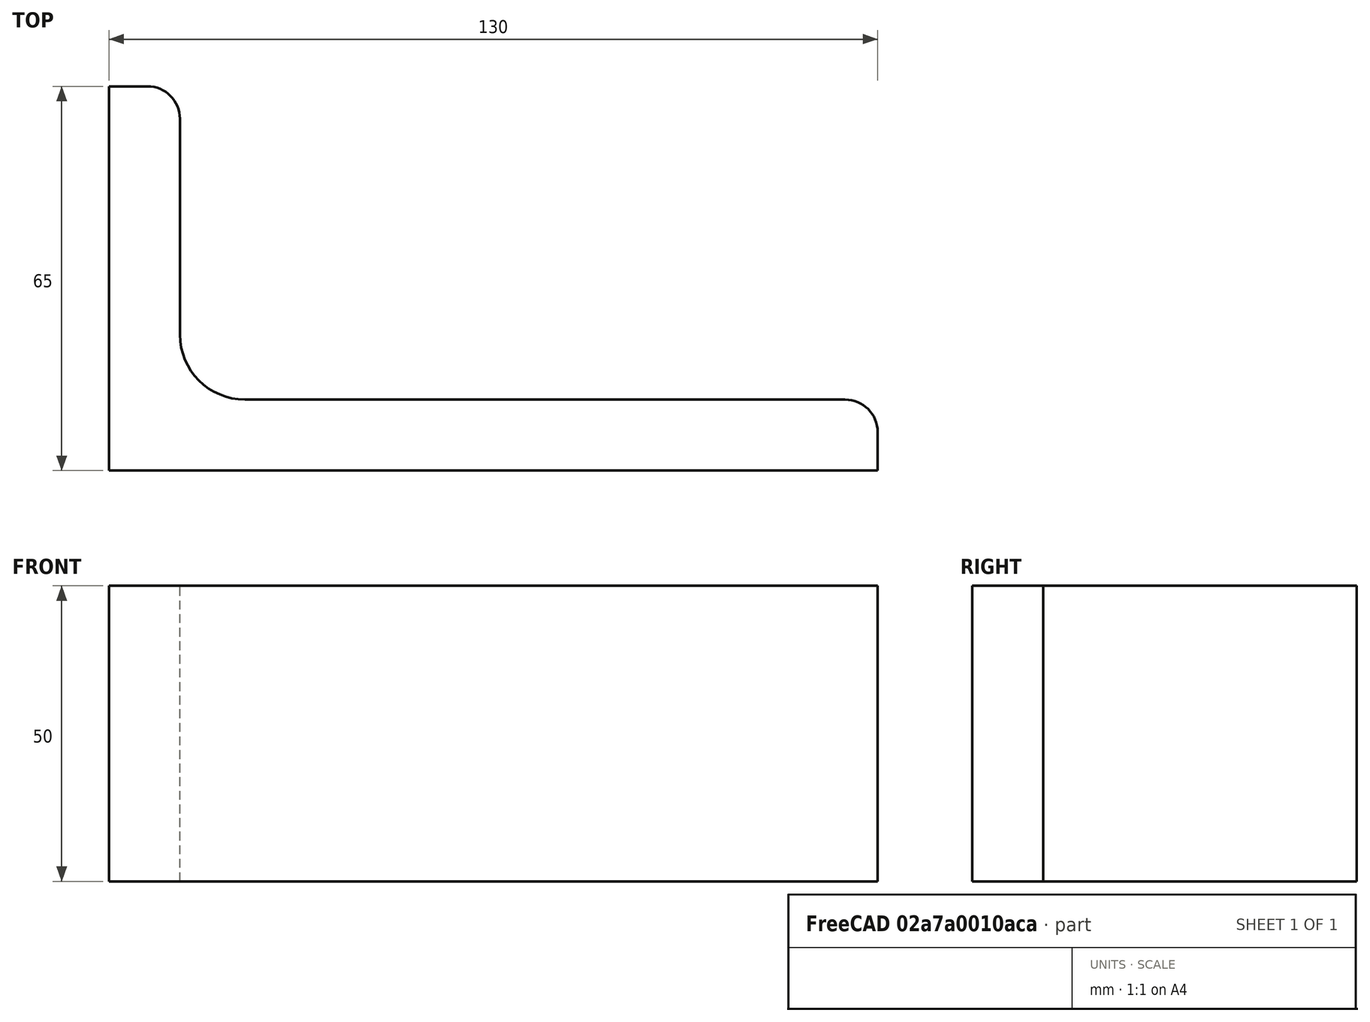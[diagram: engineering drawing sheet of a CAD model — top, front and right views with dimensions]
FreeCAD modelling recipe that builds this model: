
FCSTD DOCUMENT  (FreeCAD 0.15R4671 (Git))
Label: Angle Bar 130x65x12 EN10056 S235JR
License: All rights reserved
LicenseURL: http://en.wikipedia.org/wiki/All_rights_reserved
objects: Sketcher::SketchObject×1, Part::Extrusion×1
note: 2 computed .brp shape members not serialized (recipe doc carries the construction recipe); baked Part::Feature solids carry a one-line shape summary decoded from their .brp

FEATURE [Sketcher::SketchObject] Sketch
  sketch-geometry (9):
    g0: LineSegment StartX=0 StartY=0 StartZ=0 EndX=130 EndY=0 EndZ=0
    g1: LineSegment StartX=130 StartY=0 StartZ=0 EndX=130 EndY=6.5 EndZ=0
    g2: LineSegment StartX=124.5 StartY=12 StartZ=0 EndX=23 EndY=12 EndZ=0
    g3: LineSegment StartX=0 StartY=0 StartZ=0 EndX=0 EndY=65 EndZ=0
    g4: LineSegment StartX=0 StartY=65 StartZ=0 EndX=6.5 EndY=65 EndZ=0
    g5: LineSegment StartX=12 StartY=59.5 StartZ=0 EndX=12 EndY=23 EndZ=0
    g6: ArcOfCircle CenterX=23 CenterY=23 CenterZ=0 NormalX=0 NormalY=0 NormalZ=1 Radius=11 StartAngle=3.14159 EndAngle=4.71239
    g7: ArcOfCircle CenterX=6.5 CenterY=59.5 CenterZ=0 NormalX=0 NormalY=0 NormalZ=1 Radius=5.5 StartAngle=0 EndAngle=1.5708
    g8: ArcOfCircle CenterX=124.5 CenterY=6.5 CenterZ=0 NormalX=0 NormalY=0 NormalZ=1 Radius=5.5 StartAngle=0 EndAngle=1.5708
  constraints (23):
    c: Coincident(g0,g-1)
    c: Horizontal(g0)
    c: Coincident(g1,g0)
    c: Vertical(g1)
    c: Horizontal(g2)
    c: Coincident(g3,g-1)
    c: Vertical(g3)
    c: Coincident(g4,g3)
    c: Horizontal(g4)
    c: Vertical(g5)
    c: Tangent(g5,g6) = -1.5708
    c: Tangent(g2,g6) = 1.5708
    c: Tangent(g4,g7) = 1.5708
    c: Tangent(g5,g7) = 1.5708
    c: Tangent(g2,g8) = -1.5708
    c: Tangent(g1,g8) = -1.5708
    c: DistanceX(g0) = 130
    c: DistanceY(g3) = 65
    c: DistanceY(g0,g2) = 12
    c: DistanceX(g3,g5) = 12
    c: Radius(g6) = 11
    c: Radius(g8) = 5.5
    c: Radius(g7) = 5.5
FEATURE [Part::Extrusion] Extrude  label="Angle Bar 130x65x12 EN10056 S235JR"
  Base = -> Sketch
  Dir = (0,0,50)
  Solid = true
